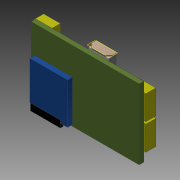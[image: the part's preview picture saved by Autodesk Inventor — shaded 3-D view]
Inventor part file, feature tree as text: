
AUTODESK INVENTOR PART (.ipt)
format: ipt  version: 2014 (Build 180170000, 170)  size: 256,512 bytes
history: native  units: mm
features: sketch x9, extrude x7, projected_geometry x4, other x2, plane x1, loft x1, chamfer x1, fillet x1
ambient origin geometry x8: Origin, YZ Plane, XZ Plane, XY Plane, X Axis, Y Axis, Z Axis, Center Point
bodies: Volumenkörper1 (feature_tree), Volumenkörper2 (feature_tree)
feature tree (26):
  other  "Platine"
  extrude  "JST"  Depth=26.0mm
  extrude  "Led"  Depth=15.0mm
  extrude  "USB"  Depth=6.2mm
  plane  "Arbeitsebene1"
  loft  "Erhebung1"
  extrude  "Slot"  Depth=3.6mm
  extrude  "Card"  Depth=0.8mm
  chamfer  "FaseUSB"  Distance=3.7mm
  fillet  "Rundung1"  Radius=12.0mm
  extrude  "JST1"  Depth=0.7mm
  extrude  "JST2"  Depth=1.7mm
  sketch  "Skizze_Platine"  dims[d23=1.0mm d24=0.7mm d25=1.7mm d26=0.5mm d28=0.5mm d29=1.1mm d30=0.0mm d31=5.0mm d33=20.5mm d34=7.5mm d35=4.3mm d36=2.8mm d37=0.0mm d41=0.6mm d42=0.2mm d43=0.3mm d44=0.0mm d45=90.0deg d46=0.0mm d47=90.0deg d48=1.3mm d49=0.6mm d50=14.0mm d51=15.2mm d52=1.0mm d53=2.5mm d54=1.85mm d55=0.0mm d56=0.8mm d57=1.0mm d58=0.2mm d60=2.6mm d61=0.0mm d62=1.5mm d63=2.0mm d64=45.0deg d65=0.5mm d66=0.4mm d67=6.0mm d68=0.0mm d69=0.4mm d70=5.5mm d71=0.0mm]
  sketch  "Skizze2"  dims[d0=40.0mm d1=26.0mm]
  sketch  "Skizze3"  dims[d2=1.7mm d3=0.0mm d4=15.0mm]
  sketch  "Skizze4"  dims[d5=0.6mm d6=6.2mm]
  sketch  "Skizze6"  dims[d7=0.8mm d8=0.6mm]
  projected_geometry  "Projizierte Kontur1"
  other  "Kanten1"
  sketch  "Skizze7"  dims[d9=9.0mm d14=3.6mm]
  sketch  "Skizze8"  dims[d15=3.6mm d17=0.8mm]
  sketch  "Skizze9"  dims[d18=6.2mm]
  projected_geometry  "Projizierte Kontur2"
  projected_geometry  "Projizierte Kontur3"
  sketch  "Skizze10"  dims[d19=9.0mm d20=3.7mm d21=0.0mm d22=12.0mm]
  projected_geometry  "Projizierte Kontur4"
